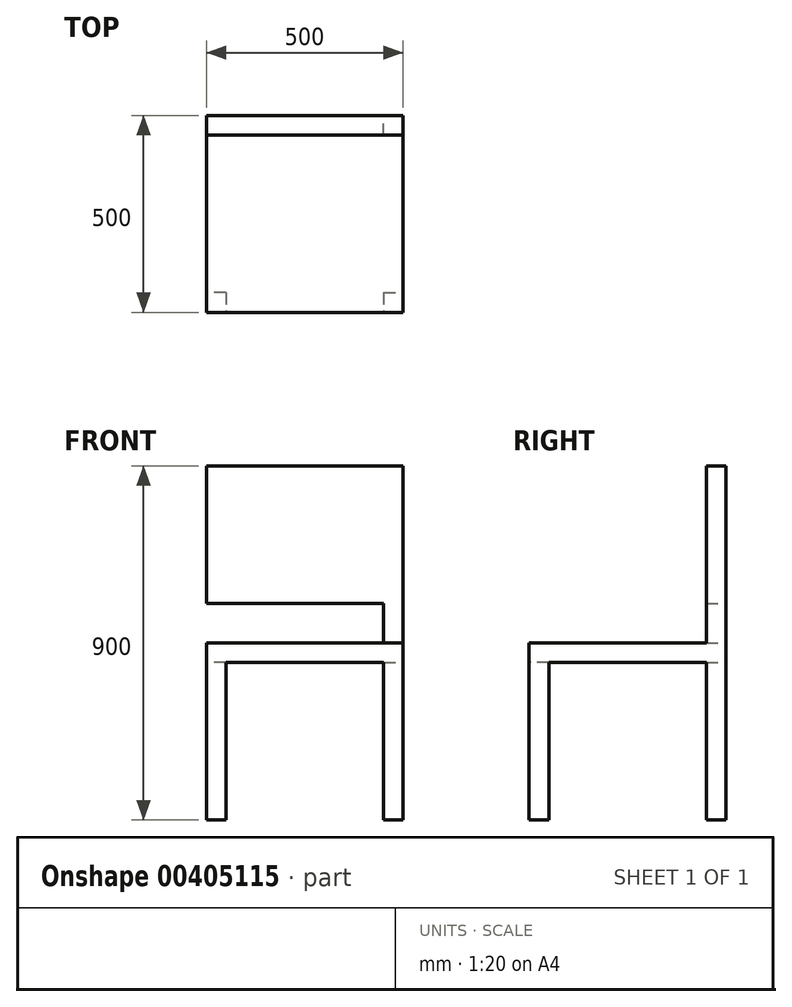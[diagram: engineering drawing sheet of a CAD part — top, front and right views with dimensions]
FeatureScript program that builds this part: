
annotation { "Feature Type Name" : "Feature", "Feature Type Description" : "" }
export const myFeature = defineFeature(function(context is Context, id is Id, definition is map)
    precondition{}
    {
        {
            var Q0;
            Q0=qCreatedBy(makeId("Top.planeOp"),FACE);
            var sketch = newSketch(context, id + "F0", { "sketchPlane" : qUnion([Q0])});
            skLineSegment(sketch, "E0.bottom", {"start": v(-250, 250) * mm, "end": v(250, 250) * mm});
            skLineSegment(sketch, "E0.top", {"start": v(-250, -250) * mm, "end": v(250, -250) * mm});
            skLineSegment(sketch, "E0.left", {"start": v(-250, 250) * mm, "end": v(-250, -250) * mm});
            skLineSegment(sketch, "E0.right", {"start": v(250, 250) * mm, "end": v(250, -250) * mm});
            skLineSegment(sketch, "E1.bottom", {"start": v(-250, 250) * mm, "end": v(-200, 250) * mm});
            skLineSegment(sketch, "E1.top", {"start": v(-250, 200) * mm, "end": v(-200, 200) * mm});
            skLineSegment(sketch, "E1.left", {"start": v(-250, 250) * mm, "end": v(-250, 200) * mm});
            skLineSegment(sketch, "E1.right", {"start": v(-200, 250) * mm, "end": v(-200, 200) * mm});
            skLineSegment(sketch, "E2.bottom", {"start": v(-200, 200) * mm, "end": v(200, 200) * mm});
            skLineSegment(sketch, "E2.top", {"start": v(-200, -200) * mm, "end": v(200, -200) * mm});
            skLineSegment(sketch, "E2.left", {"start": v(-200, 200) * mm, "end": v(-200, -200) * mm});
            skLineSegment(sketch, "E2.right", {"start": v(200, 200) * mm, "end": v(200, -200) * mm});
            skLineSegment(sketch, "E3.bottom", {"start": v(200, 200) * mm, "end": v(250, 200) * mm});
            skLineSegment(sketch, "E3.top", {"start": v(200, 250) * mm, "end": v(250, 250) * mm});
            skLineSegment(sketch, "E3.left", {"start": v(200, 200) * mm, "end": v(200, 250) * mm});
            skLineSegment(sketch, "E3.right", {"start": v(250, 200) * mm, "end": v(250, 250) * mm});
            skLineSegment(sketch, "E4.bottom", {"start": v(200, -200) * mm, "end": v(250, -200) * mm});
            skLineSegment(sketch, "E4.top", {"start": v(200, -250) * mm, "end": v(250, -250) * mm});
            skLineSegment(sketch, "E4.left", {"start": v(200, -200) * mm, "end": v(200, -250) * mm});
            skLineSegment(sketch, "E4.right", {"start": v(250, -200) * mm, "end": v(250, -250) * mm});
            skLineSegment(sketch, "E5.bottom", {"start": v(-200, -200) * mm, "end": v(-250, -200) * mm});
            skLineSegment(sketch, "E5.top", {"start": v(-200, -250) * mm, "end": v(-250, -250) * mm});
            skLineSegment(sketch, "E5.left", {"start": v(-200, -200) * mm, "end": v(-200, -250) * mm});
            skLineSegment(sketch, "E5.right", {"start": v(-250, -200) * mm, "end": v(-250, -250) * mm});
            skSolve(sketch);
        }
        {
            var Q0;
            Q0=makeQuery(id+"F0.imprint","IMPRINT",FACE,{"disambiguationData":[TD([[makeQuery(id+"F0.imprint","IMPRINT",EDGE,{"derivedFrom":sQuery(id+"F0.wireOp",EDGE,"E3.bottom")}),1.0]])]});
            var Q1;
            Q1=makeQuery(id+"F0.imprint","IMPRINT",FACE,{"disambiguationData":[TD([[makeQuery(id+"F0.imprint","IMPRINT",EDGE,{"derivedFrom":sQuery(id+"F0.wireOp",EDGE,"E1.bottom")}),-1.0]])]});
            var Q2;
            Q2=makeQuery(id+"F0.imprint","IMPRINT",FACE,{"disambiguationData":[TD([[makeQuery(id+"F0.imprint","IMPRINT",EDGE,{"derivedFrom":sQuery(id+"F0.wireOp",EDGE,"E5.bottom")}),1.0]])]});
            var Q3;
            Q3=makeQuery(id+"F0.imprint","IMPRINT",FACE,{"disambiguationData":[TD([[makeQuery(id+"F0.imprint","IMPRINT",EDGE,{"derivedFrom":sQuery(id+"F0.wireOp",EDGE,"E4.bottom")}),-1.0]])]});
            extrude(context, id + "F1", {"entities" : qUnion([Q0, Q1, Q2, Q3]), "depth" : 400 * mm});
        }
        {
            var Q0;
            Q0=makeQuery(id+"F0.imprint","IMPRINT",FACE,{"disambiguationData":[TD([[makeQuery(id+"F0.imprint","IMPRINT",EDGE,{"derivedFrom":sQuery(id+"F0.wireOp",EDGE,"E0.left")}),1.0]])]});
            var Q1;
            Q1=makeQuery(id+"F0.imprint","IMPRINT",FACE,{"disambiguationData":[TD([[makeQuery(id+"F0.imprint","IMPRINT",EDGE,{"derivedFrom":sQuery(id+"F0.wireOp",EDGE,"E2.bottom")}),-1.0]])]});
            var Q2;
            Q2=makeQuery(id+"F0.imprint","IMPRINT",FACE,{"disambiguationData":[TD([[makeQuery(id+"F0.imprint","IMPRINT",EDGE,{"derivedFrom":sQuery(id+"F0.wireOp",EDGE,"E0.bottom")}),-1.0]])]});
            var Q3;
            Q3=makeQuery(id+"F0.imprint","IMPRINT",FACE,{"disambiguationData":[TD([[makeQuery(id+"F0.imprint","IMPRINT",EDGE,{"derivedFrom":sQuery(id+"F0.wireOp",EDGE,"E0.right")}),-1.0]])]});
            var Q4;
            Q4=makeQuery(id+"F0.imprint","IMPRINT",FACE,{"disambiguationData":[TD([[makeQuery(id+"F0.imprint","IMPRINT",EDGE,{"derivedFrom":sQuery(id+"F0.wireOp",EDGE,"E0.top")}),1.0]])]});
            var Q5;
            Q5=makeQuery(id+"F0.imprint","IMPRINT",FACE,{"disambiguationData":[TD([[makeQuery(id+"F0.imprint","IMPRINT",EDGE,{"derivedFrom":sQuery(id+"F0.wireOp",EDGE,"E5.bottom")}),1.0]])]});
            var Q6;
            Q6=makeQuery(id+"F0.imprint","IMPRINT",FACE,{"disambiguationData":[TD([[makeQuery(id+"F0.imprint","IMPRINT",EDGE,{"derivedFrom":sQuery(id+"F0.wireOp",EDGE,"E1.bottom")}),-1.0]])]});
            var Q7;
            Q7=makeQuery(id+"F0.imprint","IMPRINT",FACE,{"disambiguationData":[TD([[makeQuery(id+"F0.imprint","IMPRINT",EDGE,{"derivedFrom":sQuery(id+"F0.wireOp",EDGE,"E3.bottom")}),1.0]])]});
            var Q8;
            Q8=makeQuery(id+"F0.imprint","IMPRINT",FACE,{"disambiguationData":[TD([[makeQuery(id+"F0.imprint","IMPRINT",EDGE,{"derivedFrom":sQuery(id+"F0.wireOp",EDGE,"E4.bottom")}),-1.0]])]});
            extrude(context, id + "F2", {"entities" : qUnion([Q0, Q1, Q2, Q3, Q4, Q5, Q6, Q7, Q8]), "operationType" : NewBodyOperationType.ADD, "depth" : 450 * mm, "hasSecondDirection" : true, "secondDirectionOppositeDirection" : false, "secondDirectionDepth" : 400 * mm});
        }
        {
            var Q0;
            Q0=makeQuery(id+"F0.imprint","IMPRINT",FACE,{"disambiguationData":[TD([[makeQuery(id+"F0.imprint","IMPRINT",EDGE,{"derivedFrom":sQuery(id+"F0.wireOp",EDGE,"E3.bottom")}),1.0]])]});
            var Q1;
            Q1=makeQuery(id+"F0.imprint","IMPRINT",FACE,{"disambiguationData":[TD([[makeQuery(id+"F0.imprint","IMPRINT",EDGE,{"derivedFrom":sQuery(id+"F0.wireOp",EDGE,"E1.bottom")}),-1.0]])]});
            extrude(context, id + "F3", {"entities" : qUnion([Q0, Q1]), "operationType" : NewBodyOperationType.ADD, "depth" : 550 * mm, "hasSecondDirection" : true, "secondDirectionOppositeDirection" : false, "secondDirectionDepth" : 450 * mm});
        }
        {
            var Q0;
            Q0=makeQuery(id+"F0.imprint","IMPRINT",FACE,{"disambiguationData":[TD([[makeQuery(id+"F0.imprint","IMPRINT",EDGE,{"derivedFrom":sQuery(id+"F0.wireOp",EDGE,"E0.bottom")}),-1.0]])]});
            var Q1;
            Q1=makeQuery(id+"F0.imprint","IMPRINT",FACE,{"disambiguationData":[TD([[makeQuery(id+"F0.imprint","IMPRINT",EDGE,{"derivedFrom":sQuery(id+"F0.wireOp",EDGE,"E3.bottom")}),1.0]])]});
            var Q2;
            Q2=makeQuery(id+"F0.imprint","IMPRINT",FACE,{"disambiguationData":[TD([[makeQuery(id+"F0.imprint","IMPRINT",EDGE,{"derivedFrom":sQuery(id+"F0.wireOp",EDGE,"E1.bottom")}),-1.0]])]});
            extrude(context, id + "F4", {"entities" : qUnion([Q0, Q1, Q2]), "operationType" : NewBodyOperationType.ADD, "depth" : 900 * mm, "hasSecondDirection" : true, "secondDirectionOppositeDirection" : false, "secondDirectionDepth" : 550 * mm});
        }
    });
